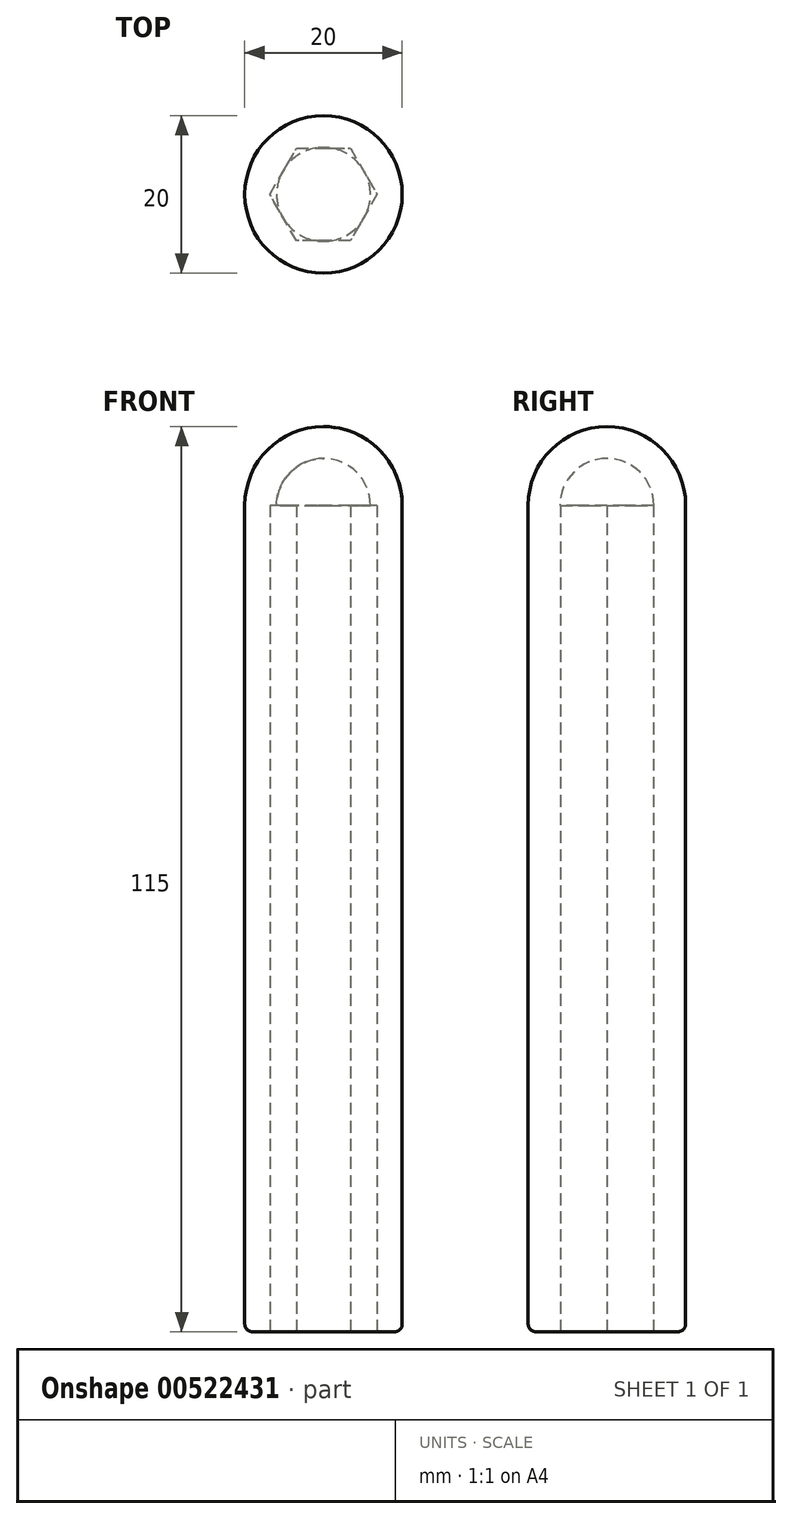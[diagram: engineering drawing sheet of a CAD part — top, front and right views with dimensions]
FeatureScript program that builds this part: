
annotation { "Feature Type Name" : "Feature", "Feature Type Description" : "" }
export const myFeature = defineFeature(function(context is Context, id is Id, definition is map)
    precondition{}
    {
        {
            var Q0;
            Q0=qCreatedBy(makeId("Top.planeOp"),FACE);
            var sketch = newSketch(context, id + "F0", { "sketchPlane" : qUnion([Q0])});
            skCircle(sketch, "E0.cCircle", {"center": v(0, 0) * mm, "radius": 5.9 * mm, "construction": true});
            skLineSegment(sketch, "E0.0", {"start": v(3.4, -5.9) * mm, "end": v(-3.4, -5.9) * mm});
            skLineSegment(sketch, "E0.1", {"start": v(-3.4, -5.9) * mm, "end": v(-6.81, 0) * mm});
            skLineSegment(sketch, "E0.2", {"start": v(-6.81, 0) * mm, "end": v(-3.4, 5.9) * mm});
            skLineSegment(sketch, "E0.3", {"start": v(-3.4, 5.9) * mm, "end": v(3.4, 5.9) * mm});
            skLineSegment(sketch, "E0.4", {"start": v(3.4, 5.9) * mm, "end": v(6.81, 0) * mm});
            skLineSegment(sketch, "E0.5", {"start": v(6.81, 0) * mm, "end": v(3.4, -5.9) * mm});
            skPoint(sketch, "E0.0.midPoint", {"position": v(0, -5.9) * mm});
            skCircle(sketch, "E1", {"center": v(0, 0) * mm, "radius": 10 * mm});
            skSolve(sketch);
        }
        {
            var Q0;
            Q0=makeQuery(id+"F0.imprint","IMPRINT",FACE,{"disambiguationData":[TD([[makeQuery(id+"F0.imprint","IMPRINT",EDGE,{"derivedFrom":sQuery(id+"F0.wireOp",EDGE,"E0.0")}),1.0]])]});
            extrude(context, id + "F1", {"entities" : qUnion([Q0]), "depth" : 105 * mm, "offsetDistance" : 25 * mm});
        }
        {
            var Q0;
            Q0=qCreatedBy(makeId("Front.planeOp"),FACE);
            var sketch = newSketch(context, id + "F2", { "sketchPlane" : qUnion([Q0])});
            skArc(sketch, "E2", {"start": v(0, 115) * mm, "mid": v(-7.07, 112.07) * mm, "end": v(-10, 105) * mm});
            skLineSegment(sketch, "E3", {"start": v(-10, 105) * mm, "end": v(-5.95, 105) * mm});
            skLineSegment(sketch, "E4", {"start": v(0, 115) * mm, "end": v(0, 110.95) * mm});
            skPoint(sketch, "E5.orphan", {"position": v(0, 118.36) * mm});
            skArc(sketch, "E6", {"start": v(0, 110.95) * mm, "mid": v(-4.2, 109.2) * mm, "end": v(-5.95, 105) * mm});
            skLineSegment(sketch, "E7.trimOffspring", {"start": v(0, 105) * mm, "end": v(10, 105) * mm});
            skSolve(sketch);
        }
        {
            var Q0;
            {var subQ0=sQuery(id+"F2.wireOp",EDGE,"E2");Q0=makeQuery(id+"F2.imprint","IMPRINT",FACE,{"disambiguationData":[TD([[makeQuery(id+"F2.imprint","IMPRINT",EDGE,{"derivedFrom":subQ0}),1.0]])]});}
            var Q1;
            Q1=sQuery(id+"F2.wireOp",EDGE,"E4");
            revolve(context, id + "F3", {"operationType" : NewBodyOperationType.ADD, "entities" : qUnion([Q0]), "axis" : qUnion([Q1]), "revolveType" : RevolveType.FULL});
        }
        {
            var Q0;
            Q0=makeQuery(id+"F1.opExtrude","CAP_EDGE",EDGE,{"disambiguationData":[OSD([sQuery(id+"F0.wireOp",EDGE,"E1")])],"isStart":true});
            fillet(context, id + "F4", {"entities" : qUnion([Q0]), "radius" : 1 * mm, "tangentPropagation" : true, "allowEdgeOverflow" : false});
        }
    });
